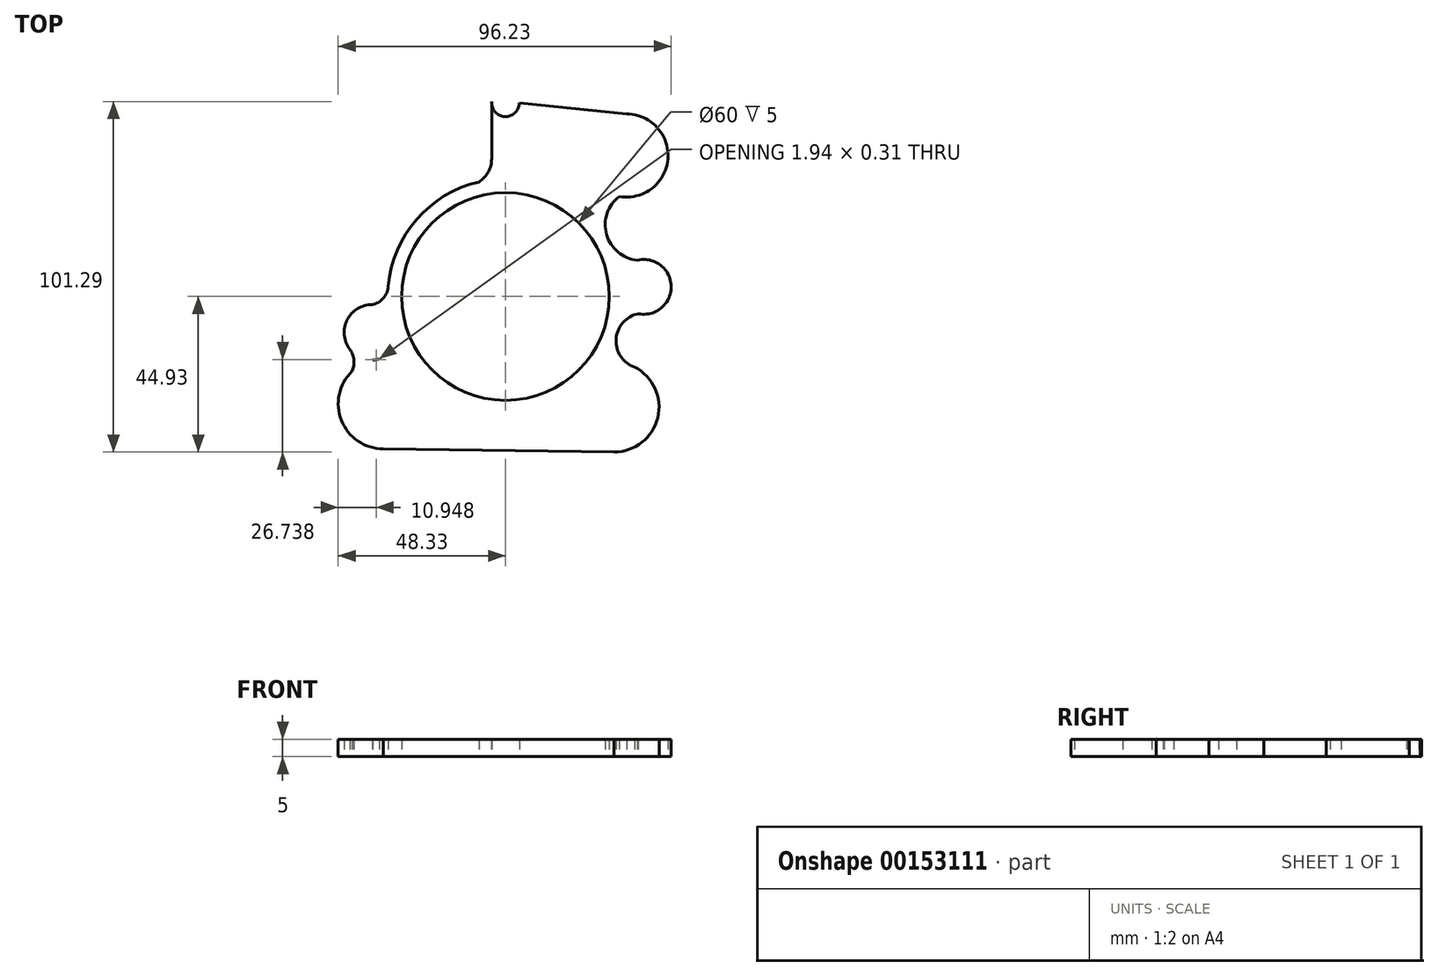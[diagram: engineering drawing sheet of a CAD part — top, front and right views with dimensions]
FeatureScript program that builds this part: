
annotation { "Feature Type Name" : "Feature", "Feature Type Description" : "" }
export const myFeature = defineFeature(function(context is Context, id is Id, definition is map)
    precondition{}
    {
        {
            var Q0;
            Q0=qCreatedBy(makeId("Top.planeOp"),FACE);
            var sketch = newSketch(context, id + "F0", { "sketchPlane" : qUnion([Q0])});
            skCircle(sketch, "E0", {"center": v(0, 0) * mm, "radius": 30 * mm});
            skCircle(sketch, "E1", {"center": v(0, 0) * mm, "radius": 34 * mm});
            skCircle(sketch, "E2", {"center": v(0, 56) * mm, "radius": 4 * mm});
            skLineSegment(sketch, "E3", {"start": v(-3.98, 56.36) * mm, "end": v(-3.98, 39.83) * mm});
            skArc(sketch, "E4", {"start": v(-7.6, 33.14) * mm, "mid": v(-4.95, 36.03) * mm, "end": v(-3.98, 39.83) * mm});
            skLineSegment(sketch, "E5", {"start": v(4, 56) * mm, "end": v(35, 52.74) * mm});
            skCircle(sketch, "E6", {"center": v(35, 40.74) * mm, "radius": 12 * mm});
            skLineSegment(sketch, "E7", {"start": v(0, 0) * mm, "end": v(14.98, -37.09) * mm});
            skLineSegment(sketch, "E8", {"start": v(0, 0) * mm, "end": v(7.63, 39.27) * mm});
            skCircle(sketch, "E9", {"center": v(7.63, 39.27) * mm, "radius": 4 * mm});
            skCircle(sketch, "E10", {"center": v(-38.64, -10.35) * mm, "radius": 4 * mm});
            skCircle(sketch, "E11", {"center": v(14.98, -37.09) * mm, "radius": 4 * mm});
            skLineSegment(sketch, "E12", {"start": v(0, 0) * mm, "end": v(-38.64, -10.35) * mm});
            skLineSegment(sketch, "E13", {"start": v(0, 0) * mm, "end": v(39.98, 2.8) * mm});
            skCircle(sketch, "E14", {"center": v(39.9, 2.8) * mm, "radius": 4 * mm});
            skLineSegment(sketch, "E15", {"start": v(0, 0) * mm, "end": v(0, 40.87) * mm});
            skCircle(sketch, "E16", {"center": v(-38.64, -10.35) * mm, "radius": 8 * mm});
            skCircle(sketch, "E17", {"center": v(39.98, 2.8) * mm, "radius": 7.92 * mm});
            skArc(sketch, "E18", {"start": v(32.87, 28.93) * mm, "mid": v(29.23, 17.93) * mm, "end": v(38.13, 10.5) * mm});
            skArc(sketch, "E19", {"start": v(38.4, -4.97) * mm, "mid": v(31.97, -12.27) * mm, "end": v(37.35, -20.38) * mm});
            skCircle(sketch, "E20", {"center": v(31.39, -31.93) * mm, "radius": 13 * mm});
            skCircle(sketch, "E21", {"center": v(-35.33, -31) * mm, "radius": 13 * mm});
            skLineSegment(sketch, "E22", {"start": v(-35.33, -44) * mm, "end": v(31.39, -44.93) * mm});
            skArc(sketch, "E23", {"start": v(-44.31, -21.6) * mm, "mid": v(-43.81, -18.34) * mm, "end": v(-44.96, -15.25) * mm});
            skArc(sketch, "E24", {"start": v(-38.54, -2.35) * mm, "mid": v(-35.32, -0.5) * mm, "end": v(-33.87, 2.92) * mm});
            skSolve(sketch);
        }
        {
            var Q0;
            {var subQ4=sQuery(id+"F0.wireOp",EDGE,"E4");Q0=makeQuery(id+"F0.imprint","IMPRINT",FACE,{"disambiguationData":[TD([[makeQuery(id+"F0.imprint","IMPRINT",EDGE,{"derivedFrom":subQ4}),-1.0]])]});}
            var Q1;
            {var subQ3=sQuery(id+"F0.wireOp",EDGE,"E8");var subQ5=sQuery(id+"F0.wireOp",EDGE,"E0");var subQ6=makeQuery(id+"F0.imprint","INTERSECT",VERTEX,{"derivedFrom":[subQ5,subQ3]});Q1=makeQuery(id+"F0.imprint","IMPRINT",FACE,{"disambiguationData":[TD([[makeQuery(id+"F0.imprint","IMPRINT",EDGE,{"disambiguationData":[TD([[subQ6,1.0]])],"derivedFrom":subQ5}),-1.0]])]});}
            var Q2;
            Q2=makeQuery(id+"F0.imprint","IMPRINT",FACE,{"disambiguationData":[TD([[makeQuery(id+"F0.imprint","IMPRINT",EDGE,{"derivedFrom":sQuery(id+"F0.wireOp",EDGE,"E14")}),-1.0]])]});
            var Q3;
            Q3=makeQuery(id+"F0.imprint","IMPRINT",FACE,{"disambiguationData":[TD([[makeQuery(id+"F0.imprint","IMPRINT",EDGE,{"derivedFrom":sQuery(id+"F0.wireOp",EDGE,"E14")}),1.0]])]});
            var Q4;
            {var subQ0=sQuery(id+"F0.wireOp",EDGE,"E18");var subQ1=sQuery(id+"F0.wireOp",EDGE,"E1");var subQ2=makeQuery(id+"F0.imprint","INTERSECT",VERTEX,{"disambiguationData":[OD(0.0)],"derivedFrom":[subQ1,subQ0]});Q4=makeQuery(id+"F0.imprint","IMPRINT",FACE,{"disambiguationData":[TD([[makeQuery(id+"F0.imprint","IMPRINT",EDGE,{"disambiguationData":[TD([[subQ2,1.0]])],"derivedFrom":subQ1}),-1.0]])]});}
            var Q5;
            {var subQ0=sQuery(id+"F0.wireOp",EDGE,"E6");var subQ1=makeQuery(id+"F0.imprint","INTERSECT",VERTEX,{"derivedFrom":[sQuery(id+"F0.wireOp",EDGE,"E5"),subQ0]});Q5=makeQuery(id+"F0.imprint","IMPRINT",FACE,{"disambiguationData":[TD([[makeQuery(id+"F0.imprint","IMPRINT",EDGE,{"disambiguationData":[TD([[subQ1,-1.0]])],"derivedFrom":subQ0}),1.0]])]});}
            var Q6;
            Q6=makeQuery(id+"F0.imprint","IMPRINT",FACE,{"disambiguationData":[TD([[makeQuery(id+"F0.imprint","IMPRINT",EDGE,{"derivedFrom":sQuery(id+"F0.wireOp",EDGE,"E9")}),1.0]])]});
            var Q7;
            {var subQ0=sQuery(id+"F0.wireOp",EDGE,"E3");var subQ1=sQuery(id+"F0.wireOp",EDGE,"E2");var subQ2=makeQuery(id+"F0.imprint","INTERSECT",VERTEX,{"disambiguationData":[OD(0.0)],"derivedFrom":[subQ1,subQ0]});Q7=makeQuery(id+"F0.imprint","IMPRINT",FACE,{"disambiguationData":[TD([[makeQuery(id+"F0.imprint","IMPRINT",EDGE,{"disambiguationData":[TD([[subQ2,1.0]])],"derivedFrom":subQ1}),1.0]])]});}
            var Q8;
            {var subQ0=sQuery(id+"F0.wireOp",EDGE,"E8");var subQ1=sQuery(id+"F0.wireOp",EDGE,"E0");var subQ2=makeQuery(id+"F0.imprint","INTERSECT",VERTEX,{"derivedFrom":[subQ1,subQ0]});Q8=makeQuery(id+"F0.imprint","IMPRINT",FACE,{"disambiguationData":[TD([[makeQuery(id+"F0.imprint","IMPRINT",EDGE,{"disambiguationData":[TD([[subQ2,-1.0]])],"derivedFrom":subQ1}),-1.0]])]});}
            var Q9;
            {var subQ5=sQuery(id+"F0.wireOp",EDGE,"E15");var subQ7=sQuery(id+"F0.wireOp",EDGE,"E0");var subQ8=makeQuery(id+"F0.imprint","INTERSECT",VERTEX,{"derivedFrom":[subQ7,subQ5]});Q9=makeQuery(id+"F0.imprint","IMPRINT",FACE,{"disambiguationData":[TD([[makeQuery(id+"F0.imprint","IMPRINT",EDGE,{"disambiguationData":[TD([[subQ8,-1.0]])],"derivedFrom":subQ7}),-1.0]])]});}
            var Q10;
            Q10=makeQuery(id+"F0.imprint","IMPRINT",FACE,{"disambiguationData":[TD([[makeQuery(id+"F0.imprint","IMPRINT",EDGE,{"derivedFrom":sQuery(id+"F0.wireOp",EDGE,"E10")}),-1.0]])]});
            var Q11;
            {var subQ0=sQuery(id+"F0.wireOp",EDGE,"E24");var subQ1=sQuery(id+"F0.wireOp",EDGE,"E1");var subQ2=makeQuery(id+"F0.imprint","INTERSECT",VERTEX,{"disambiguationData":[OD(1.0)],"derivedFrom":[subQ1,subQ0]});Q11=makeQuery(id+"F0.imprint","IMPRINT",FACE,{"disambiguationData":[TD([[makeQuery(id+"F0.imprint","IMPRINT",EDGE,{"disambiguationData":[TD([[subQ2,-1.0]])],"derivedFrom":subQ1}),-1.0]])]});}
            var Q12;
            Q12=makeQuery(id+"F0.imprint","IMPRINT",FACE,{"disambiguationData":[TD([[makeQuery(id+"F0.imprint","IMPRINT",EDGE,{"derivedFrom":sQuery(id+"F0.wireOp",EDGE,"E10")}),1.0]])]});
            var Q13;
            {var subQ0=sQuery(id+"F0.wireOp",EDGE,"E12");var subQ1=sQuery(id+"F0.wireOp",EDGE,"E1");var subQ2=makeQuery(id+"F0.imprint","INTERSECT",VERTEX,{"derivedFrom":[subQ1,subQ0]});Q13=makeQuery(id+"F0.imprint","IMPRINT",FACE,{"disambiguationData":[TD([[makeQuery(id+"F0.imprint","IMPRINT",EDGE,{"disambiguationData":[TD([[subQ2,1.0]])],"derivedFrom":subQ1}),1.0]])]});}
            var Q14;
            {var subQ11=sQuery(id+"F0.wireOp",EDGE,"E13");var subQ13=sQuery(id+"F0.wireOp",EDGE,"E0");var subQ14=makeQuery(id+"F0.imprint","INTERSECT",VERTEX,{"derivedFrom":[subQ13,subQ11]});Q14=makeQuery(id+"F0.imprint","IMPRINT",FACE,{"disambiguationData":[TD([[makeQuery(id+"F0.imprint","IMPRINT",EDGE,{"disambiguationData":[TD([[subQ14,1.0]])],"derivedFrom":subQ13}),-1.0]])]});}
            var Q15;
            {var subQ0=sQuery(id+"F0.wireOp",EDGE,"E13");var subQ1=sQuery(id+"F0.wireOp",EDGE,"E1");var subQ2=makeQuery(id+"F0.imprint","INTERSECT",VERTEX,{"derivedFrom":[subQ1,subQ0]});Q15=makeQuery(id+"F0.imprint","IMPRINT",FACE,{"disambiguationData":[TD([[makeQuery(id+"F0.imprint","IMPRINT",EDGE,{"disambiguationData":[TD([[subQ2,1.0]])],"derivedFrom":subQ1}),1.0]])]});}
            var Q16;
            {var subQ0=sQuery(id+"F0.wireOp",EDGE,"E13");var subQ1=sQuery(id+"F0.wireOp",EDGE,"E1");var subQ2=makeQuery(id+"F0.imprint","INTERSECT",VERTEX,{"derivedFrom":[subQ1,subQ0]});Q16=makeQuery(id+"F0.imprint","IMPRINT",FACE,{"disambiguationData":[TD([[makeQuery(id+"F0.imprint","IMPRINT",EDGE,{"disambiguationData":[TD([[subQ2,-1.0]])],"derivedFrom":subQ1}),1.0]])]});}
            var Q17;
            {var subQ0=sQuery(id+"F0.wireOp",EDGE,"E19");var subQ1=sQuery(id+"F0.wireOp",EDGE,"E1");var subQ2=makeQuery(id+"F0.imprint","INTERSECT",VERTEX,{"disambiguationData":[OD(0.0)],"derivedFrom":[subQ1,subQ0]});Q17=makeQuery(id+"F0.imprint","IMPRINT",FACE,{"disambiguationData":[TD([[makeQuery(id+"F0.imprint","IMPRINT",EDGE,{"disambiguationData":[TD([[subQ2,1.0]])],"derivedFrom":subQ1}),-1.0]])]});}
            var Q18;
            {var subQ0=sQuery(id+"F0.wireOp",EDGE,"E19");var subQ1=sQuery(id+"F0.wireOp",EDGE,"E1");var subQ2=makeQuery(id+"F0.imprint","INTERSECT",VERTEX,{"disambiguationData":[OD(1.0)],"derivedFrom":[subQ1,subQ0]});Q18=makeQuery(id+"F0.imprint","IMPRINT",FACE,{"disambiguationData":[TD([[makeQuery(id+"F0.imprint","IMPRINT",EDGE,{"disambiguationData":[TD([[subQ2,-1.0]])],"derivedFrom":subQ1}),-1.0]])]});}
            var Q19;
            Q19=makeQuery(id+"F0.imprint","IMPRINT",FACE,{"disambiguationData":[TD([[makeQuery(id+"F0.imprint","IMPRINT",EDGE,{"derivedFrom":sQuery(id+"F0.wireOp",EDGE,"E11")}),1.0]])]});
            var Q20;
            Q20=makeQuery(id+"F0.imprint","IMPRINT",FACE,{"disambiguationData":[TD([[makeQuery(id+"F0.imprint","IMPRINT",EDGE,{"derivedFrom":sQuery(id+"F0.wireOp",EDGE,"E11")}),-1.0]])]});
            var Q21;
            {var subQ1=sQuery(id+"F0.wireOp",EDGE,"E20");var subQ3=sQuery(id+"F0.wireOp",EDGE,"E1");var subQ4=makeQuery(id+"F0.imprint","INTERSECT",VERTEX,{"disambiguationData":[OD(0.0)],"derivedFrom":[subQ3,subQ1]});Q21=makeQuery(id+"F0.imprint","IMPRINT",FACE,{"disambiguationData":[TD([[makeQuery(id+"F0.imprint","IMPRINT",EDGE,{"disambiguationData":[TD([[subQ4,-1.0]])],"derivedFrom":subQ3}),-1.0]])]});}
            var Q22;
            {var subQ0=sQuery(id+"F0.wireOp",EDGE,"E20");var subQ1=sQuery(id+"F0.wireOp",EDGE,"E1");var subQ2=makeQuery(id+"F0.imprint","INTERSECT",VERTEX,{"disambiguationData":[OD(0.0)],"derivedFrom":[subQ1,subQ0]});Q22=makeQuery(id+"F0.imprint","IMPRINT",FACE,{"disambiguationData":[TD([[makeQuery(id+"F0.imprint","IMPRINT",EDGE,{"disambiguationData":[TD([[subQ2,-1.0]])],"derivedFrom":subQ1}),1.0]])]});}
            var Q23;
            {var subQ3=sQuery(id+"F0.wireOp",EDGE,"E0");var subQ8=sQuery(id+"F0.wireOp",EDGE,"E12");var subQ9=makeQuery(id+"F0.imprint","INTERSECT",VERTEX,{"derivedFrom":[subQ3,subQ8]});Q23=makeQuery(id+"F0.imprint","IMPRINT",FACE,{"disambiguationData":[TD([[makeQuery(id+"F0.imprint","IMPRINT",EDGE,{"disambiguationData":[TD([[subQ9,-1.0]])],"derivedFrom":subQ3}),-1.0]])]});}
            var Q24;
            {var subQ0=sQuery(id+"F0.wireOp",EDGE,"E21");var subQ3=sQuery(id+"F0.wireOp",EDGE,"E16");var subQ4=makeQuery(id+"F0.imprint","INTERSECT",VERTEX,{"disambiguationData":[OD(0.0)],"derivedFrom":[subQ3,subQ0]});Q24=makeQuery(id+"F0.imprint","IMPRINT",FACE,{"disambiguationData":[TD([[makeQuery(id+"F0.imprint","IMPRINT",EDGE,{"disambiguationData":[TD([[subQ4,-1.0]])],"derivedFrom":subQ3}),-1.0]])]});}
            var Q25;
            {var subQ0=sQuery(id+"F0.wireOp",EDGE,"E16");var subQ1=sQuery(id+"F0.wireOp",EDGE,"E1");var subQ2=makeQuery(id+"F0.imprint","INTERSECT",VERTEX,{"disambiguationData":[OD(1.0)],"derivedFrom":[subQ1,subQ0]});Q25=makeQuery(id+"F0.imprint","IMPRINT",FACE,{"disambiguationData":[TD([[makeQuery(id+"F0.imprint","IMPRINT",EDGE,{"disambiguationData":[TD([[subQ2,-1.0]])],"derivedFrom":subQ1}),-1.0]])]});}
            var Q26;
            {var subQ0=sQuery(id+"F0.wireOp",EDGE,"E23");Q26=makeQuery(id+"F0.imprint","IMPRINT",FACE,{"disambiguationData":[TD([[makeQuery(id+"F0.imprint","IMPRINT",EDGE,{"derivedFrom":subQ0}),-1.0]])]});}
            var Q27;
            {var subQ0=sQuery(id+"F0.wireOp",EDGE,"E12");var subQ1=sQuery(id+"F0.wireOp",EDGE,"E1");var subQ2=makeQuery(id+"F0.imprint","INTERSECT",VERTEX,{"derivedFrom":[subQ1,subQ0]});Q27=makeQuery(id+"F0.imprint","IMPRINT",FACE,{"disambiguationData":[TD([[makeQuery(id+"F0.imprint","IMPRINT",EDGE,{"disambiguationData":[TD([[subQ2,-1.0]])],"derivedFrom":subQ1}),1.0]])]});}
            extrude(context, id + "F1", {"entities" : qUnion([Q0, Q1, Q2, Q3, Q4, Q5, Q6, Q7, Q8, Q9, Q10, Q11, Q12, Q13, Q14, Q15, Q16, Q17, Q18, Q19, Q20, Q21, Q22, Q23, Q24, Q25, Q26, Q27]), "depth" : 5 * mm});
        }
    });
